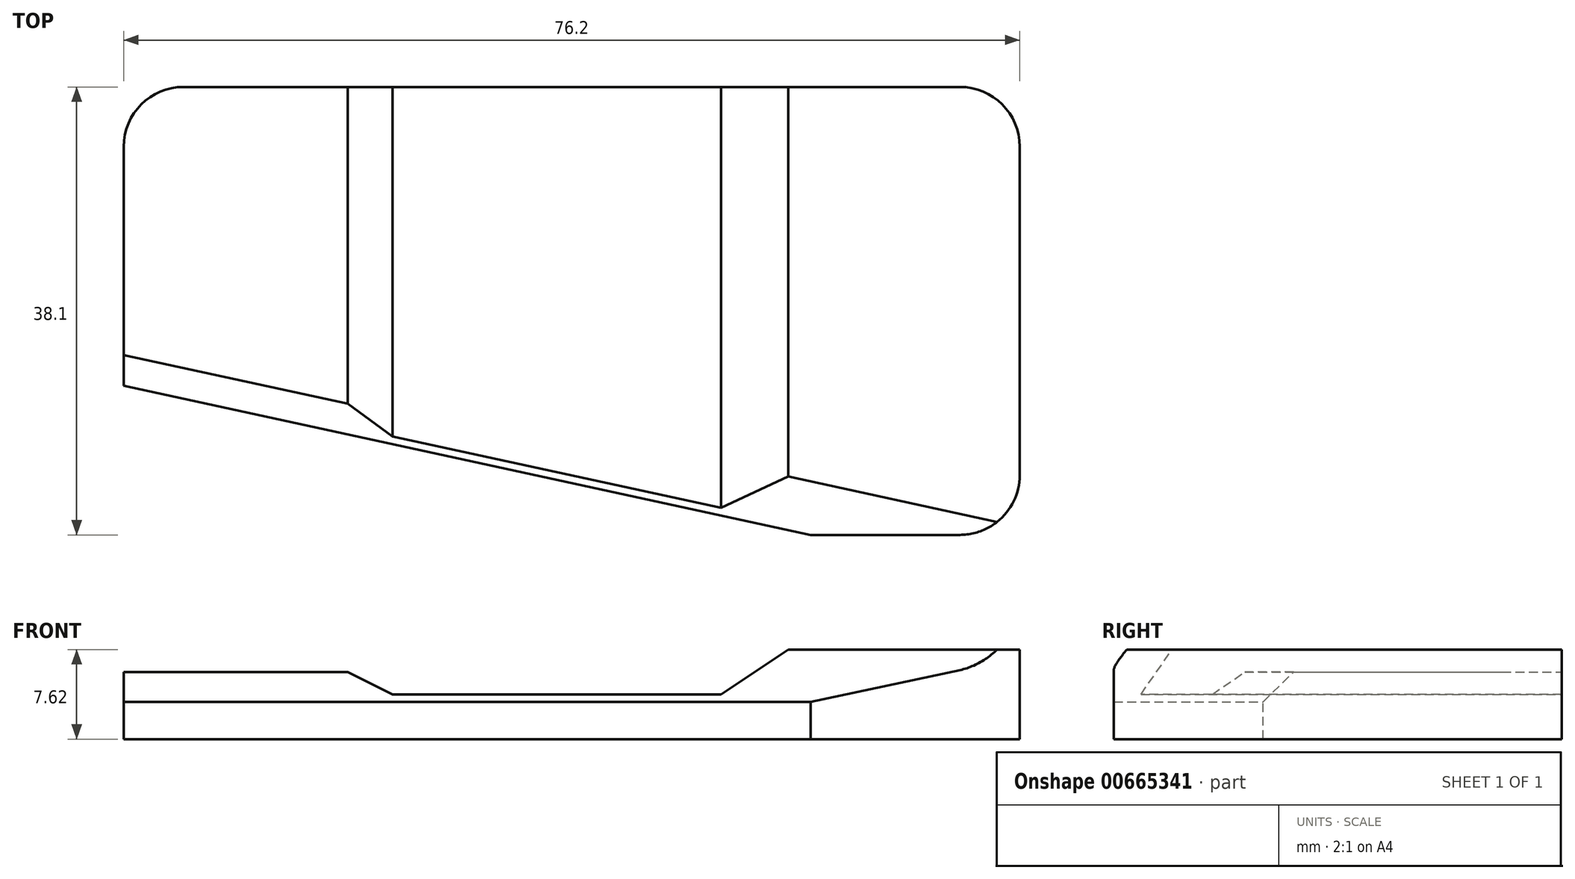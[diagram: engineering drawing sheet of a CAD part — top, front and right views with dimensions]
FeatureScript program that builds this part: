
annotation { "Feature Type Name" : "Feature", "Feature Type Description" : "" }
export const myFeature = defineFeature(function(context is Context, id is Id, definition is map)
    precondition{}
    {
        {
            var Q0;
            Q0=qCreatedBy(makeId("Top.planeOp"),FACE);
            var sketch = newSketch(context, id + "F0", { "sketchPlane" : qUnion([Q0])});
            skLineSegment(sketch, "E0.bottom", {"start": v(38.1, -19.05) * mm, "end": v(-38.1, -19.05) * mm});
            skLineSegment(sketch, "E0.top", {"start": v(38.1, 19.05) * mm, "end": v(-38.1, 19.05) * mm});
            skLineSegment(sketch, "E0.left", {"start": v(38.1, -19.05) * mm, "end": v(38.1, 19.05) * mm});
            skLineSegment(sketch, "E0.right", {"start": v(-38.1, -19.05) * mm, "end": v(-38.1, 19.05) * mm});
            skPoint(sketch, "E0.middle", {"position": v(0, 0) * mm});
            skSolve(sketch);
        }
        {
            var Q0;
            Q0=makeQuery(id+"F0.imprint","IMPRINT",FACE,{"disambiguationData":[TD([[makeQuery(id+"F0.imprint","IMPRINT",EDGE,{"derivedFrom":sQuery(id+"F0.wireOp",EDGE,"E0.bottom")}),-1.0]])]});
            extrude(context, id + "F1", {"entities" : qUnion([Q0]), "depth" : 7.62 * mm, "offsetDistance" : 25.4 * mm});
        }
        {
            var Q0;
            Q0=makeQuery(id+"F1.opExtrude","CAP_FACE",FACE,{"disambiguationData":[OSD([sQuery(id+"F0.wireOp",EDGE,"E0.bottom"),sQuery(id+"F0.wireOp",EDGE,"E0.top"),sQuery(id+"F0.wireOp",EDGE,"E0.left"),sQuery(id+"F0.wireOp",EDGE,"E0.right")])],"isStart":false});
            var sketch = newSketch(context, id + "F2", { "sketchPlane" : qUnion([Q0])});
            skLineSegment(sketch, "E1.bottom", {"start": v(20.32, -19.05) * mm, "end": v(-20.32, -19.05) * mm});
            skLineSegment(sketch, "E1.top", {"start": v(20.32, 19.05) * mm, "end": v(-20.32, 19.05) * mm});
            skLineSegment(sketch, "E1.left", {"start": v(20.32, -19.05) * mm, "end": v(20.32, 19.05) * mm});
            skLineSegment(sketch, "E1.right", {"start": v(-20.32, -19.05) * mm, "end": v(-20.32, 19.05) * mm});
            skPoint(sketch, "E1.middle", {"position": v(0, 0) * mm});
            skLineSegment(sketch, "E2.left", {"start": v(-20.32, 19.05) * mm, "end": v(-20.32, -19.05) * mm});
            skSolve(sketch);
        }
        {
            var Q0;
            {var subQ0=sQuery(id+"F2.wireOp",EDGE,"E1.left");Q0=makeQuery(id+"F2.imprint","IMPRINT",FACE,{"disambiguationData":[TD([[makeQuery(id+"F2.imprint","IMPRINT",EDGE,{"derivedFrom":subQ0}),-1.0]])]});}
            var sketch = newSketch(context, id + "F3", { "sketchPlane" : qUnion([Q0])});
            skLineSegment(sketch, "E3.0", {"start": v(-38.1, -19.05) * mm, "end": v(-38.1, 19.05) * mm});
            skLineSegment(sketch, "E4.0", {"start": v(20.32, -19.05) * mm, "end": v(-20.32, -19.05) * mm});
            skLineSegment(sketch, "E5.0", {"start": v(20.32, -19.05) * mm, "end": v(-38.1, -19.05) * mm});
            skPoint(sketch, "E6.orphan", {"position": v(38.1, -19.05) * mm});
            skLineSegment(sketch, "E7", {"start": v(-38.1, -6.35) * mm, "end": v(20.32, -19.05) * mm});
            skSolve(sketch);
        }
        {
            var Q0;
            {var subQ3=sQuery(id+"F3.wireOp",EDGE,"cd232530-1e49-4a57-8ab3-45a062eee770");Q0=makeQuery(id+"F3.imprint","IMPRINT",FACE,{"disambiguationData":[TD([[makeQuery(id+"F3.imprint","IMPRINT",EDGE,{"derivedFrom":subQ3}),-1.0]])]});}
            var Q1;
            {var subQ3=sQuery(id+"F3.wireOp",EDGE,"E7");Q1=makeQuery(id+"F3.imprint","IMPRINT",FACE,{"disambiguationData":[TD([[makeQuery(id+"F3.imprint","IMPRINT",EDGE,{"derivedFrom":subQ3}),-1.0]])]});}
            extrude(context, id + "F4", {"entities" : qUnion([Q0, Q1]), "operationType" : NewBodyOperationType.REMOVE, "endBound" : BoundingType.THROUGH_ALL, "oppositeDirection" : true, "depth" : 25.4 * mm, "offsetDistance" : 25.4 * mm});
        }
        {
            var Q0;
            Q0=makeQuery(id+"F1.opExtrude","SWEPT_FACE",FACE,{"disambiguationData":[OSD([sQuery(id+"F0.wireOp",EDGE,"E0.top")])]});
            var sketch = newSketch(context, id + "F5", { "sketchPlane" : qUnion([Q0])});
            skPoint(sketch, "E8.0", {"position": v(-20.32, 7.62) * mm});
            skPoint(sketch, "E9.0", {"position": v(20.32, 7.62) * mm});
            skLineSegment(sketch, "E10", {"start": v(-20.32, 7.62) * mm, "end": v(-20.32, 3.81) * mm});
            skLineSegment(sketch, "E11", {"start": v(20.32, 5.72) * mm, "end": v(20.32, 3.81) * mm});
            skLineSegment(sketch, "E12", {"start": v(-20.32, 3.81) * mm, "end": v(20.32, 3.81) * mm});
            skLineSegment(sketch, "E13", {"start": v(20.32, 5.72) * mm, "end": v(38.1, 5.72) * mm});
            skSolve(sketch);
        }
        {
            var Q0;
            {var subQ1=sQuery(id+"F5.wireOp",EDGE,"E10");Q0=makeQuery(id+"F5.imprint","IMPRINT",FACE,{"disambiguationData":[TD([[makeQuery(id+"F5.imprint","IMPRINT",EDGE,{"derivedFrom":subQ1}),1.0]])]});}
            extrude(context, id + "F6", {"entities" : qUnion([Q0]), "operationType" : NewBodyOperationType.REMOVE, "endBound" : BoundingType.THROUGH_ALL, "oppositeDirection" : true, "depth" : 25.4 * mm, "offsetDistance" : 25.4 * mm});
        }
        {
            var Q0;
            Q0=makeQuery(id+"F6.boolean.opBoolean","COPY",EDGE,{"derivedFrom":makeQuery(id+"F6.opExtrude","SWEPT_EDGE",EDGE,{"disambiguationData":[OSD([sQuery(id+"F5.wireOp",EDGE,"E10"),sQuery(id+"F5.wireOp",EDGE,"E12")])]})});
            chamfer(context, id + "F7", {"entities" : qUnion([Q0]), "chamferType" : ChamferType.TWO_OFFSETS, "width1" : 7.62 * mm, "oppositeDirection" : false, "width2" : 5.08 * mm, "tangentPropagation" : true});
        }
        {
            var Q0;
            Q0=makeQuery(id+"F6.boolean.opBoolean","COPY",EDGE,{"derivedFrom":makeQuery(id+"F6.opExtrude","SWEPT_EDGE",EDGE,{"disambiguationData":[OSD([sQuery(id+"F5.wireOp",EDGE,"E11"),sQuery(id+"F5.wireOp",EDGE,"E12")])]})});
            chamfer(context, id + "F8", {"entities" : qUnion([Q0]), "chamferType" : ChamferType.TWO_OFFSETS, "width1" : 2.54 * mm, "oppositeDirection" : false, "width2" : 5.08 * mm, "tangentPropagation" : true});
        }
        {
            var Q0;
            Q0=makeQuery(id+"F4.boolean.opBoolean","COPY",EDGE,{"derivedFrom":makeQuery(id+"F4.opExtrude","SWEPT_EDGE",EDGE,{"disambiguationData":[OSD([sQuery(id+"F3.wireOp",EDGE,"E3.0"),sQuery(id+"F3.wireOp",EDGE,"E7")])]})});
            var Q1;
            Q1=makeQuery(id+"F1.opExtrude","SWEPT_EDGE",EDGE,{"disambiguationData":[OSD([sQuery(id+"F0.wireOp",EDGE,"E0.top"),sQuery(id+"F0.wireOp",EDGE,"E0.right")])]});
            var Q2;
            Q2=makeQuery(id+"F1.opExtrude","SWEPT_EDGE",EDGE,{"disambiguationData":[OSD([sQuery(id+"F0.wireOp",EDGE,"E0.bottom"),sQuery(id+"F0.wireOp",EDGE,"E0.left")])]});
            var Q3;
            Q3=makeQuery(id+"F1.opExtrude","SWEPT_EDGE",EDGE,{"disambiguationData":[OSD([sQuery(id+"F0.wireOp",EDGE,"E0.top"),sQuery(id+"F0.wireOp",EDGE,"E0.left")])]});
            fillet(context, id + "F9", {"entities" : qUnion([Q0, Q1, Q2, Q3]), "radius" : 5.08 * mm, "tangentPropagation" : true, "allowEdgeOverflow" : false});
        }
        {
            var Q0;
            Q0=makeQuery(id+"F6.boolean.opBoolean","INTERSECT",EDGE,{"derivedFrom":[makeQuery(id+"F4.boolean.opBoolean","COPY",FACE,{"derivedFrom":makeQuery(id+"F4.opExtrude","SWEPT_FACE",FACE,{"disambiguationData":[OSD([sQuery(id+"F3.wireOp",EDGE,"E7")])]})}),makeQuery(id+"F6.opExtrude","SWEPT_FACE",FACE,{"disambiguationData":[OSD([sQuery(id+"F5.wireOp",EDGE,"E13")])]})]});
            chamfer(context, id + "F10", {"entities" : qUnion([Q0]), "width" : 2.54 * mm, "tangentPropagation" : true});
        }
    });
